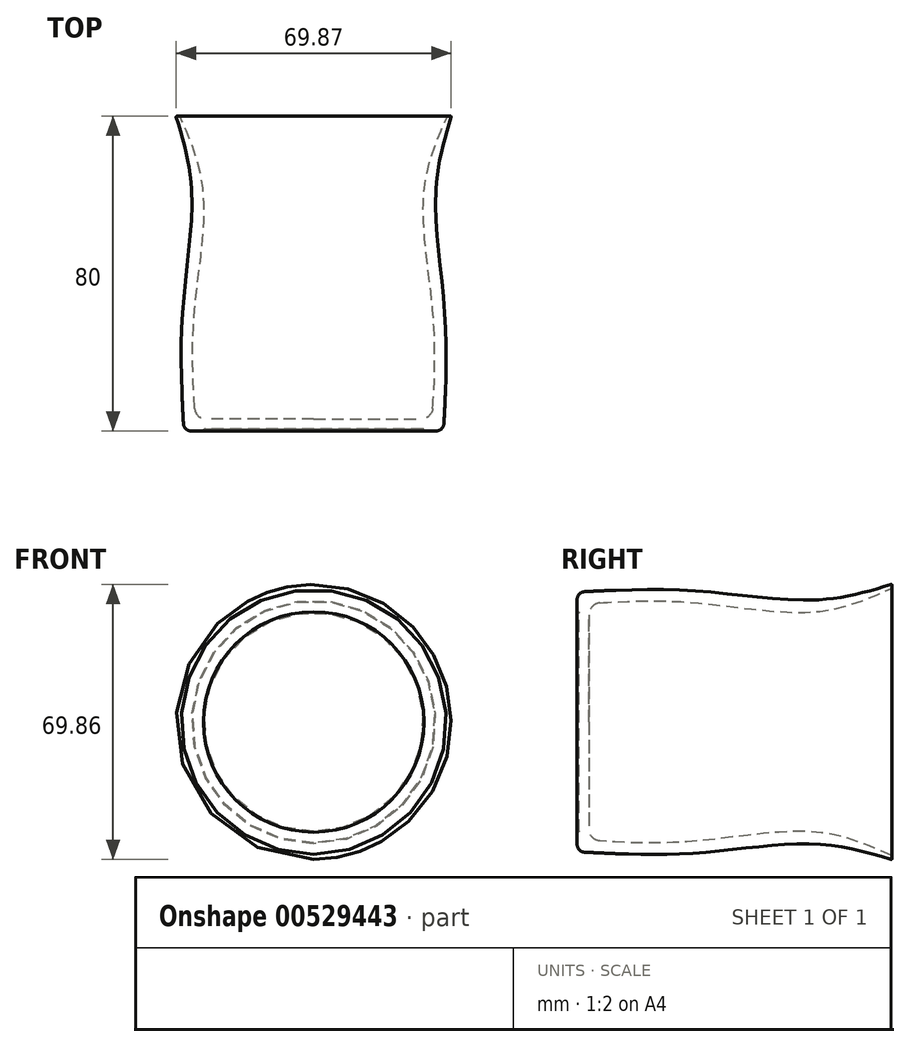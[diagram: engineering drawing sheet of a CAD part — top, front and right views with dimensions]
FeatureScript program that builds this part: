
annotation { "Feature Type Name" : "Feature", "Feature Type Description" : "" }
export const myFeature = defineFeature(function(context is Context, id is Id, definition is map)
    precondition{}
    {
        {
            var Q0;
            Q0=qCreatedBy(makeId("Top.planeOp"),FACE);
            var sketch = newSketch(context, id + "F0", { "sketchPlane" : qUnion([Q0])});
            skLineSegment(sketch, "E0", {"start": v(28.92, -11.48) * mm, "end": v(28.92, -10.98) * mm});
            skLineSegment(sketch, "E1", {"start": v(28.92, -10.98) * mm, "end": v(1.22, -10.98) * mm});
            skLineSegment(sketch, "E2", {"start": v(0.92, -11.28) * mm, "end": v(0.92, -11.28) * mm});
            skLineSegment(sketch, "E3", {"start": v(0.72, -11.48) * mm, "end": v(-2.18, -11.48) * mm});
            skLineSegment(sketch, "E4", {"start": v(-5.2, 68.52) * mm, "end": v(-5.8, 68.52) * mm});
            skFitSpline(sketch, "E5", {"points": [v(-4.08, -11.48) * mm, v(-4.38, 18.52) * mm, v(-2.08, 49.02) * mm, v(-6.08, 68.52) * mm], "startDerivative": vector(-4.3, 83.26) * mm, "endDerivative": vector(-19.18, 63.33) * mm});
            skLineSegment(sketch, "E6", {"start": v(-4.58, -1.66) * mm, "end": v(-4.54, -1.66) * mm});
            skLineSegment(sketch, "E7", {"start": v(-2.18, -11.48) * mm, "end": v(-1.58, -11.48) * mm});
            skLineSegment(sketch, "E8", {"start": v(-4.1, -8.48) * mm, "end": v(-4.08, -8.48) * mm});
            skLineSegment(sketch, "E9", {"start": v(28.92, -10.98) * mm, "end": v(28.92, -8.48) * mm});
            skLineSegment(sketch, "E10", {"start": v(1.68, -8.48) * mm, "end": v(28.92, -8.48) * mm});
            skLineSegment(sketch, "E11", {"start": v(-5.8, 68.52) * mm, "end": v(-5.2, 68.52) * mm});
            skFitSpline(sketch, "E12", {"points": [v(-5.08, 68.52) * mm, v(0.92, 49.02) * mm, v(-1.38, 18.55) * mm, v(-1.58, -1.63) * mm, v(-1.08, -8.48) * mm], "startDerivative": vector(30.49, -68.52) * mm, "endDerivative": vector(3.43, -39.56) * mm});
            skArc(sketch, "E13.filletArc", {"start": v(-4.17, -9.59) * mm, "mid": v(-3.55, -10.93) * mm, "end": v(-2.18, -11.48) * mm});
            skArc(sketch, "E14.filletArc", {"start": v(-1.3, -5.72) * mm, "mid": v(-0.35, -7.69) * mm, "end": v(1.68, -8.48) * mm});
            skPoint(sketch, "E15.end.orphan", {"position": v(2.92, 49.02) * mm});
            skPoint(sketch, "E16.orphan", {"position": v(-4.08, 68.52) * mm});
            skPoint(sketch, "E17.visualSharp", {"position": v(0.92, -10.98) * mm});
            skArc(sketch, "E17.filletArc", {"start": v(1.22, -10.98) * mm, "mid": v(1.01, -11.07) * mm, "end": v(0.92, -11.28) * mm});
            skPoint(sketch, "E18.visualSharp", {"position": v(0.92, -11.48) * mm});
            skArc(sketch, "E18.filletArc", {"start": v(0.72, -11.48) * mm, "mid": v(0.87, -11.42) * mm, "end": v(0.92, -11.28) * mm});
            skArc(sketch, "E19.filletArc", {"start": v(-5.8, 68.52) * mm, "mid": v(-5.97, 68.44) * mm, "end": v(-6, 68.26) * mm});
            skArc(sketch, "E20.filletArc", {"start": v(-5.02, 68.4) * mm, "mid": v(-5.1, 68.48) * mm, "end": v(-5.2, 68.52) * mm});
            skSolve(sketch);
        }
        {
            var Q0;
            Q0=makeQuery(id+"F0.imprint","IMPRINT",FACE,{"disambiguationData":[TD([[makeQuery(id+"F0.imprint","IMPRINT",EDGE,{"derivedFrom":sQuery(id+"F0.wireOp",EDGE,"E1")}),-1.0]])]});
            var Q1;
            Q1=sQuery(id+"F0.wireOp",EDGE,"E0");
            revolve(context, id + "F1", {"entities" : qUnion([Q0]), "axis" : qUnion([Q1]), "revolveType" : RevolveType.FULL});
        }
    });
